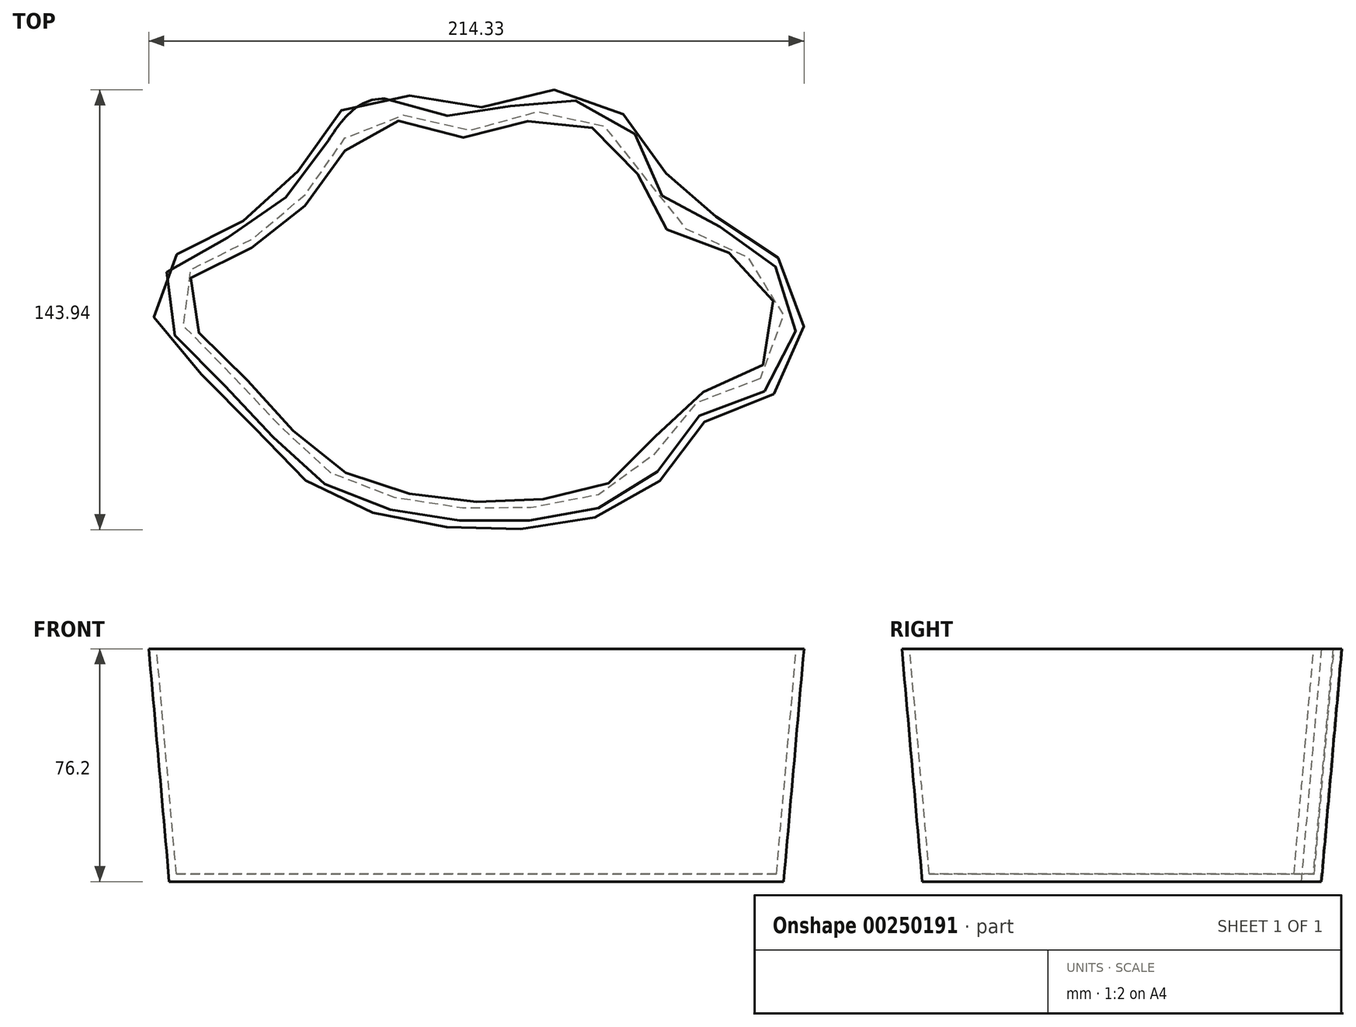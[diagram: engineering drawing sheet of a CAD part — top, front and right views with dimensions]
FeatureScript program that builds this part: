
annotation { "Feature Type Name" : "Feature", "Feature Type Description" : "" }
export const myFeature = defineFeature(function(context is Context, id is Id, definition is map)
    precondition{}
    {
        {
            var Q0;
            Q0=qCreatedBy(makeId("Top.planeOp"),FACE);
            var sketch = newSketch(context, id + "F0", { "sketchPlane" : qUnion([Q0])});
            skPoint(sketch, "E0.middle", {"position": v(0, 0) * mm});
            skPoint(sketch, "E1.visualSharp", {"position": v(-76.2, 50.8) * mm});
            skPoint(sketch, "E2.visualSharp", {"position": v(76.2, 50.8) * mm});
            skPoint(sketch, "E3.visualSharp", {"position": v(76.2, -50.8) * mm});
            skPoint(sketch, "E4.visualSharp", {"position": v(-76.2, -50.8) * mm});
            skFitSpline(sketch, "E5", {"points": [v(-76.2, 25.4) * mm, v(-50.8, 50.8) * mm, v(-35.08, 67.16) * mm, v(-7.68, 61.01) * mm, v(22.53, 67.67) * mm, v(50.8, 50.8) * mm, v(56.07, 33.87) * mm, v(76.2, 25.4) * mm, v(97.3, 3.14) * mm, v(90.12, -20.16) * mm, v(76.2, -25.4) * mm, v(61.2, -34.5) * mm, v(50.8, -50.8) * mm, v(5.38, -62.92) * mm, v(-50.8, -50.8) * mm, v(-76.2, -25.4) * mm, v(-103.18, 7.75) * mm, v(-76.2, 25.4) * mm]});
            skSolve(sketch);
        }
        {
            var Q0;
            Q0=makeQuery(id+"F0.imprint","IMPRINT",FACE,{"disambiguationData":[TD([[makeQuery(id+"F0.imprint","IMPRINT",EDGE,{"derivedFrom":sQuery(id+"F0.wireOp",EDGE,"E5")}),-1.0]])]});
            extrude(context, id + "F1", {"entities" : qUnion([Q0]), "depth" : 76.2 * mm, "hasDraft" : true, "draftAngle" : 5 * degree});
        }
        {
            var Q0;
            Q0=makeQuery(id+"F1.opExtrude","CAP_FACE",FACE,{"disambiguationData":[OSD([sQuery(id+"F0.wireOp",EDGE,"E5")])],"isStart":false});
            shell(context, id + "F2", {"entities" : qUnion([Q0]), "thickness" : 2.54 * mm});
        }
    });
